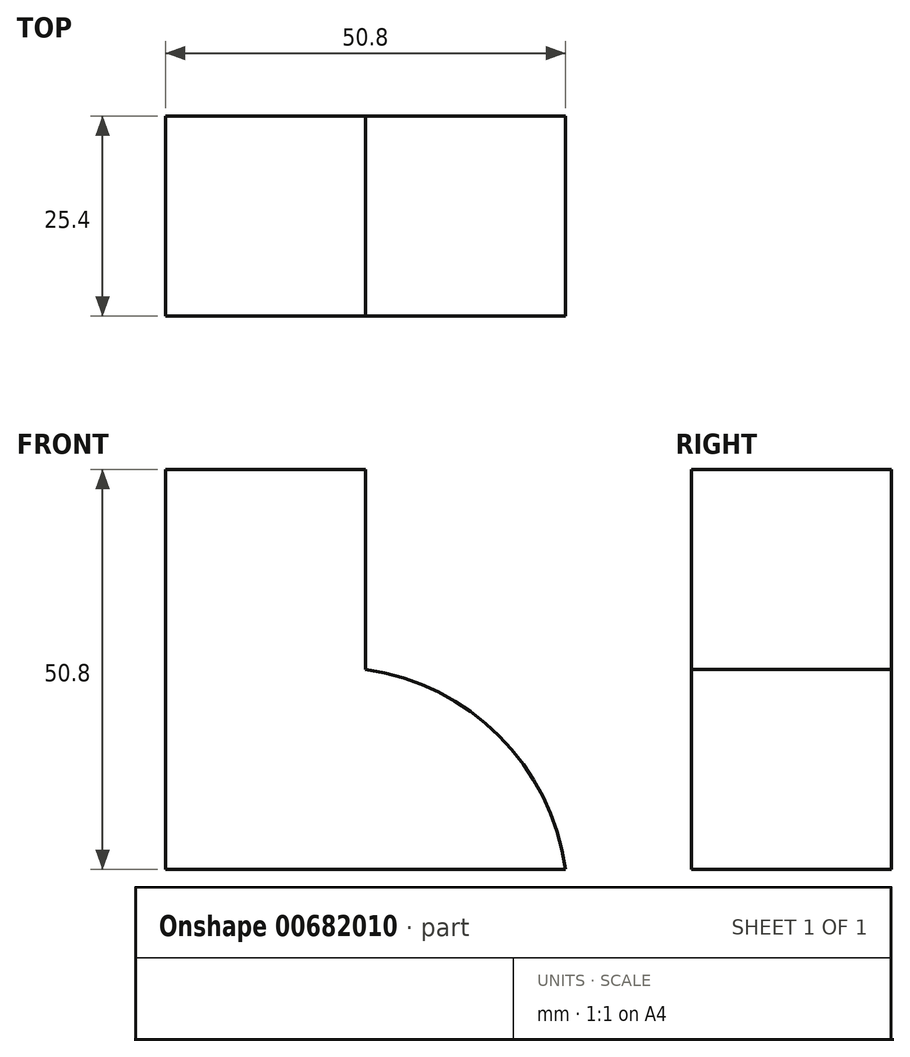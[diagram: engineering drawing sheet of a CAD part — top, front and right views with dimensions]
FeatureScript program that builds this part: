
annotation { "Feature Type Name" : "Feature", "Feature Type Description" : "" }
export const myFeature = defineFeature(function(context is Context, id is Id, definition is map)
    precondition{}
    {
        {
            var Q0;
            Q0=qCreatedBy(makeId("Front.planeOp"),FACE);
            var sketch = newSketch(context, id + "F0", { "sketchPlane" : qUnion([Q0])});
            skLineSegment(sketch, "E0", {"start": v(0, 0) * mm, "end": v(-50.8, 0) * mm});
            skLineSegment(sketch, "E1", {"start": v(-50.8, 0) * mm, "end": v(-50.8, 50.8) * mm});
            skLineSegment(sketch, "E2", {"start": v(-50.8, 50.8) * mm, "end": v(-25.4, 50.8) * mm});
            skLineSegment(sketch, "E3", {"start": v(-25.4, 50.8) * mm, "end": v(-25.4, 25.4) * mm});
            skArc(sketch, "E4", {"start": v(0, 0) * mm, "mid": v(-8.44, 16.96) * mm, "end": v(-25.4, 25.4) * mm});
            skSolve(sketch);
        }
        {
            var Q0;
            Q0=makeQuery(id+"F0.imprint","IMPRINT",FACE,{"disambiguationData":[TD([[makeQuery(id+"F0.imprint","IMPRINT",EDGE,{"derivedFrom":sQuery(id+"F0.wireOp",EDGE,"E0")}),-1.0]])]});
            extrude(context, id + "F1", {"entities" : qUnion([Q0]), "depth" : 25.4 * mm, "offsetDistance" : 25.4 * mm});
        }
    });
